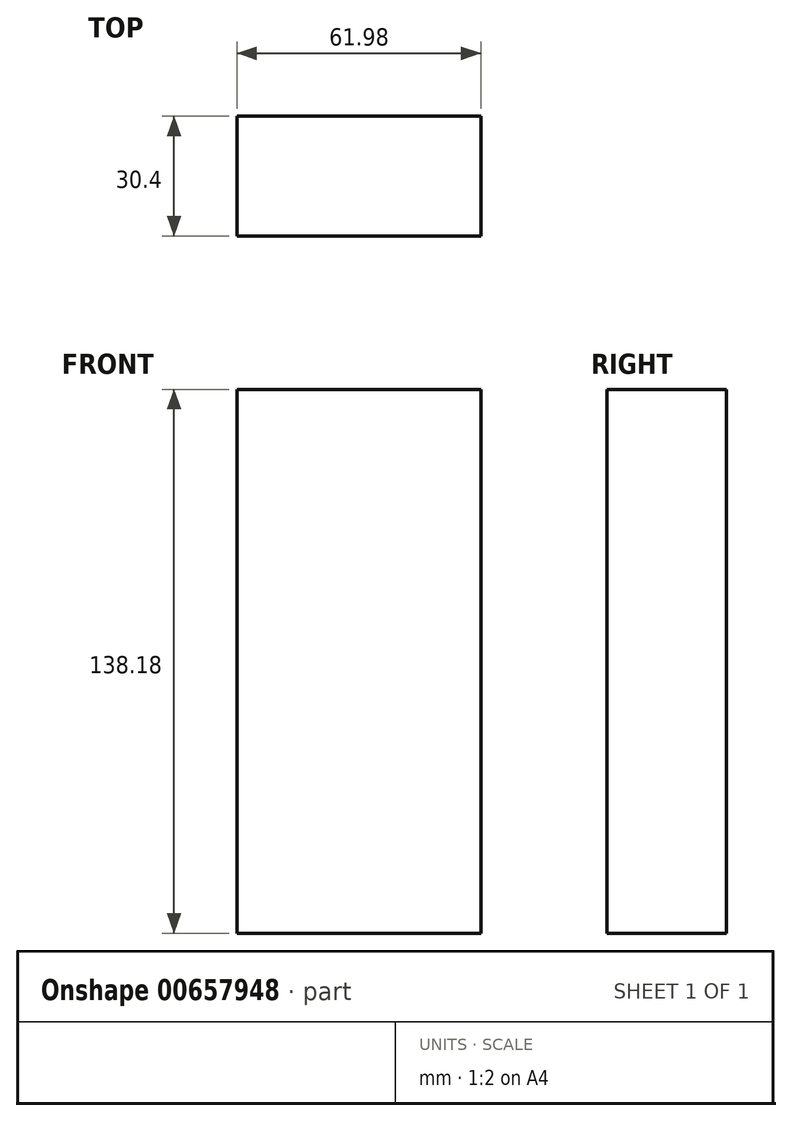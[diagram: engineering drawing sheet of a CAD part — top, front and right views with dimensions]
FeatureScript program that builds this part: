
annotation { "Feature Type Name" : "Feature", "Feature Type Description" : "" }
export const myFeature = defineFeature(function(context is Context, id is Id, definition is map)
    precondition{}
    {
        {
            var Q0;
            Q0=qCreatedBy(makeId("Front.planeOp"),FACE);
            var sketch = newSketch(context, id + "F0", { "sketchPlane" : qUnion([Q0])});
            skLineSegment(sketch, "E0.bottom", {"start": v(-168.97, 138.18) * mm, "end": v(-106.99, 138.18) * mm});
            skLineSegment(sketch, "E0.top", {"start": v(-168.97, 0) * mm, "end": v(-106.99, 0) * mm});
            skLineSegment(sketch, "E0.left", {"start": v(-168.97, 138.18) * mm, "end": v(-168.97, 0) * mm});
            skLineSegment(sketch, "E0.right", {"start": v(-106.99, 138.18) * mm, "end": v(-106.99, 0) * mm});
            skSolve(sketch);
        }
        {
            var Q0;
            Q0 = qSketchRegion(id + "F0", true);
            extrude(context, id + "F1", {"entities" : qUnion([Q0]), "depth" : 5 * mm, "offsetDistance" : 25.4 * mm});
        }
        {
            var Q0;
            Q0=makeQuery(id+"F1.opExtrude","CAP_FACE",FACE,{"disambiguationData":[OSD([sQuery(id+"F0.wireOp",EDGE,"E0.bottom"),sQuery(id+"F0.wireOp",EDGE,"E0.top"),sQuery(id+"F0.wireOp",EDGE,"E0.left"),sQuery(id+"F0.wireOp",EDGE,"E0.right")])],"isStart":true});
            var Q1;
            Q1=makeQuery(id+"F1.opExtrude","CAP_FACE",FACE,{"disambiguationData":[OSD([sQuery(id+"F0.wireOp",EDGE,"E0.bottom"),sQuery(id+"F0.wireOp",EDGE,"E0.top"),sQuery(id+"F0.wireOp",EDGE,"E0.left"),sQuery(id+"F0.wireOp",EDGE,"E0.right")])],"isStart":false});
            extrude(context, id + "F2", {"entities" : qUnion([Q0, Q1]), "operationType" : NewBodyOperationType.ADD, "depth" : 25.4 * mm, "offsetDistance" : 25.4 * mm});
        }
    });
